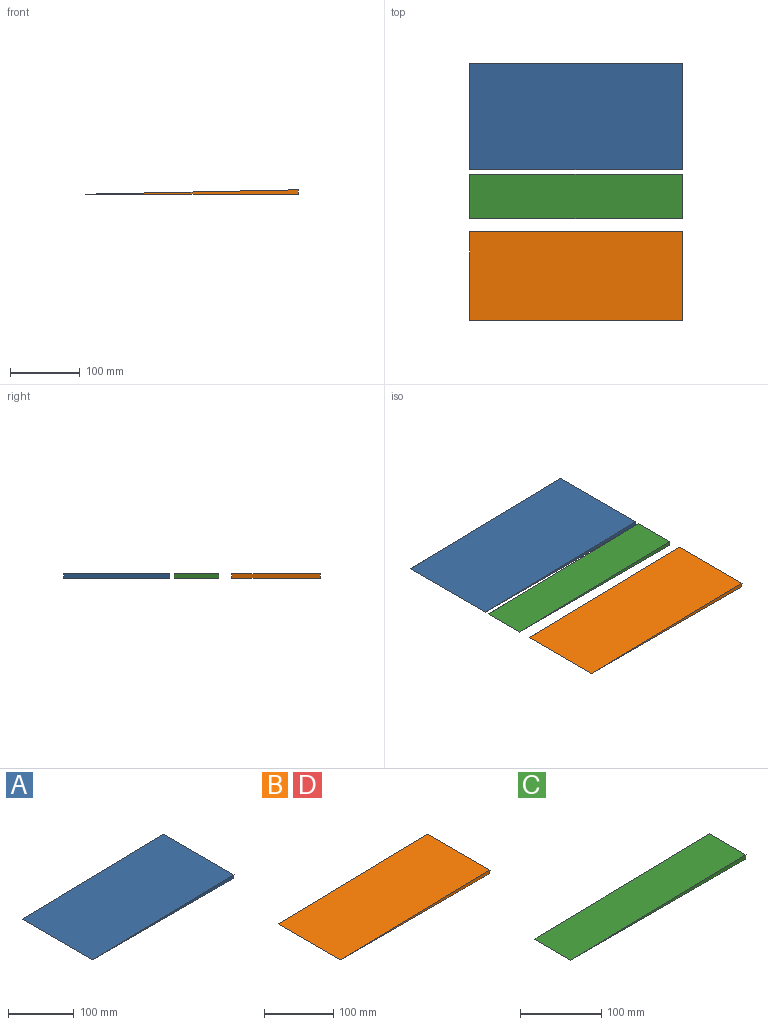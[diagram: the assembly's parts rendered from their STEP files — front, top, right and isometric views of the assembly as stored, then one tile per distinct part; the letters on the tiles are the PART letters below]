
ASSEMBLY  parts=4 mates=4
PART A: 5 faces, bbox 304.8x152.4x6.4 mm
  f0: plane 304.8x152.4mm, normal (0,0,-1), area 46451.5mm2, adj f1,f2,f3,f4
  f1: plane 152.4x6.35mm, normal (1,0,0), area 967.7mm2, adj f0,f2,f3,f4
  f2: plane 304.8x152.4mm, normal (-0.02,0,1), area 46461.6mm2, adj f0,f1,f3,f4
  f3: plane 304.8x6.35mm, normal (0,-1,0), area 967.7mm2, adj f0,f1,f2
  f4: plane 304.8x6.35mm, normal (0,1,0), area 967.7mm2, adj f0,f1,f2
PART B: 5 faces, bbox 304.8x127x6.4 mm
  f0: plane 304.8x127mm, normal (0,0,-1), area 38709.6mm2, adj f1,f2,f3,f4
  f1: plane 127x6.35mm, normal (1,0,0), area 806.5mm2, adj f0,f2,f3,f4
  f2: plane 304.8x127mm, normal (-0.02,0,1), area 38718mm2, adj f0,f1,f3,f4
  f3: plane 304.8x6.35mm, normal (0,-1,0), area 967.7mm2, adj f0,f1,f2
  f4: plane 304.8x6.35mm, normal (0,1,0), area 967.7mm2, adj f0,f1,f2
PART C: 5 faces, bbox 304.8x63.5x6.4 mm
  f0: plane 304.8x63.5mm, normal (0,0,-1), area 19354.8mm2, adj f1,f2,f3,f4
  f1: plane 63.5x6.35mm, normal (1,0,0), area 403.2mm2, adj f0,f2,f3,f4
  f2: plane 304.8x63.5mm, normal (-0.02,0,1), area 19359mm2, adj f0,f1,f3,f4
  f3: plane 304.8x6.35mm, normal (0,-1,0), area 967.7mm2, adj f0,f1,f2
  f4: plane 304.8x6.35mm, normal (0,1,0), area 967.7mm2, adj f0,f1,f2
PART D: same geometry as B
PLACE A t=(-54.71,187.88,-18.24)mm
PLACE B t=(-54.71,-53.42,-18.24)mm fixed
PLACE C t=(-54.71,29.13,-18.24)mm
PLACE D t=(-54.71,-53.42,-18.24)mm
MATE planar C.f0 <-> A.f0  axis (0,0,-1) through (-207.11,-2.62,-18.24)mm
MATE planar C.f1 <-> A.f1  axis (1,0,0) through (-54.71,-2.62,-15.07)mm
MATE planar B.f1 <-> C.f1  axis (1,0,0) through (-54.71,-116.92,-15.07)mm
MATE planar B.f0 <-> C.f0  axis (0,0,-1) through (-207.11,-116.92,-18.24)mm
